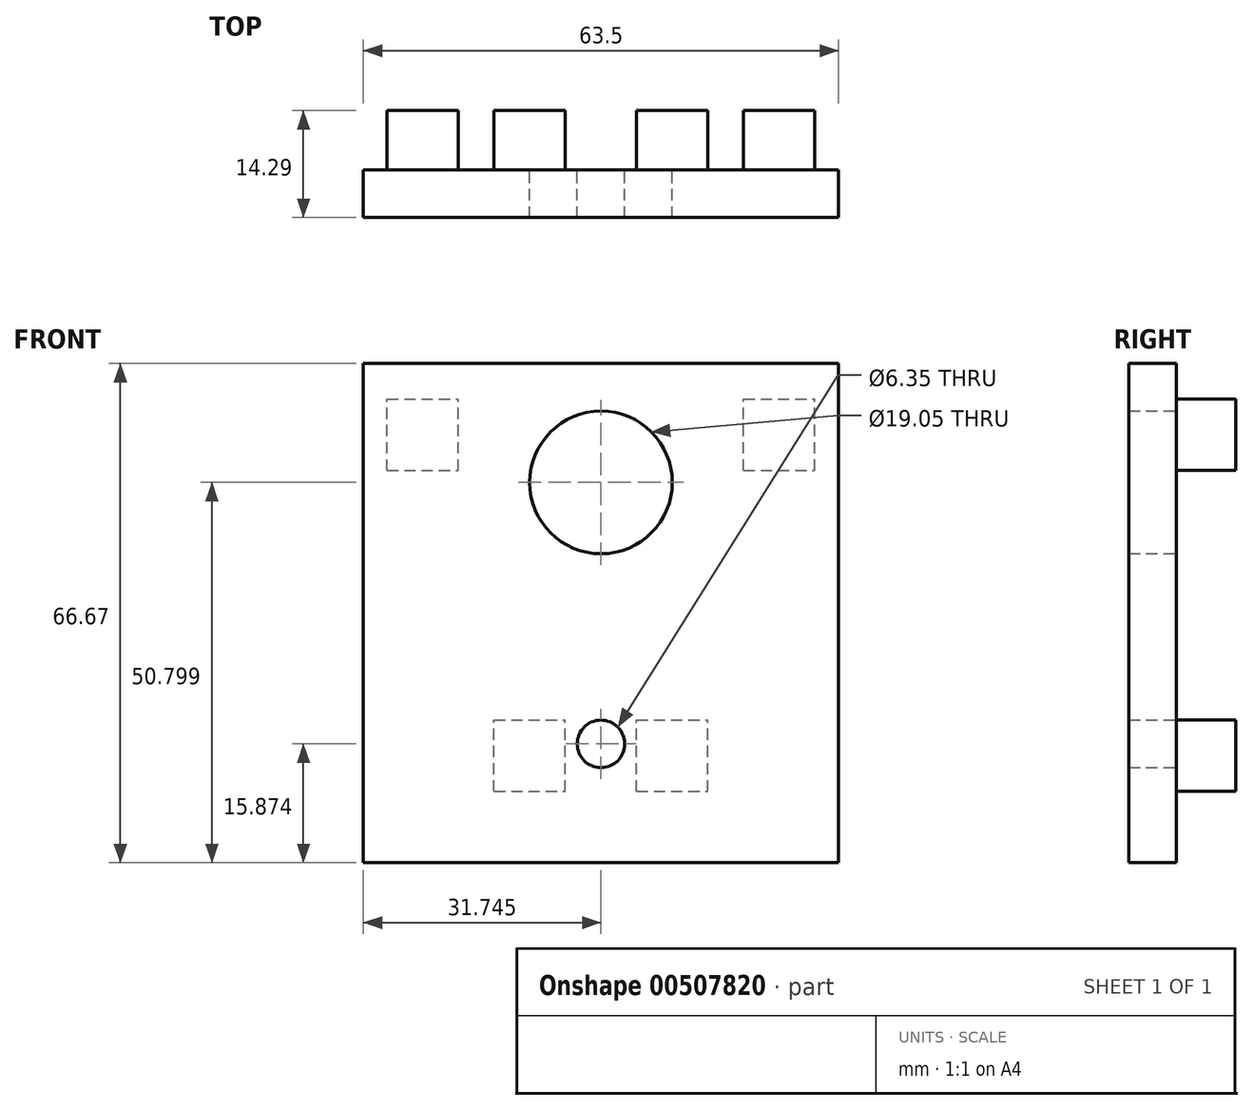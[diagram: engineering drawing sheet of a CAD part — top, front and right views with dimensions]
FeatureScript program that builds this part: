
annotation { "Feature Type Name" : "Feature", "Feature Type Description" : "" }
export const myFeature = defineFeature(function(context is Context, id is Id, definition is map)
    precondition{}
    {
        {
            var Q0;
            Q0=qCreatedBy(makeId("Front.planeOp"),FACE);
            var sketch = newSketch(context, id + "F0", { "sketchPlane" : qUnion([Q0])});
            skLineSegment(sketch, "E0.bottom", {"start": v(-27.9, 18.37) * mm, "end": v(35.6, 18.37) * mm});
            skLineSegment(sketch, "E0.top", {"start": v(-27.9, -45.13) * mm, "end": v(35.6, -45.13) * mm});
            skLineSegment(sketch, "E0.left", {"start": v(-27.9, 18.37) * mm, "end": v(-27.9, -45.13) * mm});
            skLineSegment(sketch, "E0.right", {"start": v(35.6, 18.37) * mm, "end": v(35.6, -45.13) * mm});
            skCircle(sketch, "E1", {"center": v(3.85, 2.5) * mm, "radius": 9.53 * mm});
            skLineSegment(sketch, "E2", {"start": v(-27.9, 2.5) * mm, "end": v(35.6, 2.5) * mm, "construction": true});
            skLineSegment(sketch, "E3.top", {"start": v(-27.9, -48.3) * mm, "end": v(35.6, -48.3) * mm});
            skLineSegment(sketch, "E3.left", {"start": v(-27.9, -45.13) * mm, "end": v(-27.9, -48.3) * mm});
            skLineSegment(sketch, "E3.right", {"start": v(35.6, -45.13) * mm, "end": v(35.6, -48.3) * mm});
            skLineSegment(sketch, "E4", {"start": v(-6.74, -45.13) * mm, "end": v(-6.74, -48.3) * mm});
            skLineSegment(sketch, "E5", {"start": v(14.43, -45.13) * mm, "end": v(14.43, -48.3) * mm});
            skCircle(sketch, "E6", {"center": v(3.85, -32.43) * mm, "radius": 3.18 * mm});
            skLineSegment(sketch, "E7", {"start": v(-10.44, 18.37) * mm, "end": v(-10.44, -45.13) * mm});
            skLineSegment(sketch, "E8", {"start": v(18.13, 18.37) * mm, "end": v(18.13, -45.13) * mm});
            skSolve(sketch);
        }
        {
            var Q0;
            {var subQ0=sQuery(id+"F0.wireOp",EDGE,"E3.left");Q0=makeQuery(id+"F0.imprint","IMPRINT",FACE,{"disambiguationData":[TD([[makeQuery(id+"F0.imprint","IMPRINT",EDGE,{"derivedFrom":subQ0}),1.0]])]});}
            var Q1;
            {var subQ0=sQuery(id+"F0.wireOp",EDGE,"E3.right");Q1=makeQuery(id+"F0.imprint","IMPRINT",FACE,{"disambiguationData":[TD([[makeQuery(id+"F0.imprint","IMPRINT",EDGE,{"derivedFrom":subQ0}),-1.0]])]});}
            var Q2;
            Q2=makeQuery(id+"F0.imprint","IMPRINT",FACE,{"disambiguationData":[TD([[makeQuery(id+"F0.imprint","IMPRINT",EDGE,{"derivedFrom":sQuery(id+"F0.wireOp",EDGE,"E0.bottom")}),-1.0]])]});
            var Q3;
            Q3=makeQuery(id+"F0.imprint","IMPRINT",FACE,{"disambiguationData":[TD([[makeQuery(id+"F0.imprint","IMPRINT",EDGE,{"derivedFrom":sQuery(id+"F0.wireOp",EDGE,"E1")}),-1.0]])]});
            var Q4;
            {var subQ0=sQuery(id+"F0.wireOp",EDGE,"E4");Q4=makeQuery(id+"F0.imprint","IMPRINT",FACE,{"disambiguationData":[TD([[makeQuery(id+"F0.imprint","IMPRINT",EDGE,{"derivedFrom":subQ0}),1.0]])]});}
            extrude(context, id + "F1", {"entities" : qUnion([Q0, Q1, Q2, Q3, Q4]), "endBound" : BoundingType.SYMMETRIC, "depth" : 6.35 * mm, "offsetDistance" : 25.4 * mm});
        }
        {
            var Q0;
            Q0=makeQuery(id+"F1.opExtrude","CAP_FACE",FACE,{"disambiguationData":[OSD([sQuery(id+"F0.wireOp",EDGE,"E0.bottom"),sQuery(id+"F0.wireOp",EDGE,"E0.left"),sQuery(id+"F0.wireOp",EDGE,"E0.right"),sQuery(id+"F0.wireOp",EDGE,"E1"),sQuery(id+"F0.wireOp",EDGE,"E0.top"),sQuery(id+"F0.wireOp",EDGE,"E3.top"),sQuery(id+"F0.wireOp",EDGE,"E3.left"),sQuery(id+"F0.wireOp",EDGE,"E3.right"),sQuery(id+"F0.wireOp",EDGE,"E4"),sQuery(id+"F0.wireOp",EDGE,"E5"),sQuery(id+"F0.wireOp",EDGE,"E6")])],"isStart":true});
            var sketch = newSketch(context, id + "F2", { "sketchPlane" : qUnion([Q0])});
            skLineSegment(sketch, "E9", {"start": v(-3.85, 2.5) * mm, "end": v(19.97, 2.5) * mm, "construction": true});
            skLineSegment(sketch, "E10", {"start": v(-3.85, 2.5) * mm, "end": v(-27.66, 2.5) * mm, "construction": true});
            skLineSegment(sketch, "E11", {"start": v(19.97, 2.5) * mm, "end": v(19.97, 8.85) * mm, "construction": true});
            skLineSegment(sketch, "E12", {"start": v(-27.66, 2.5) * mm, "end": v(-27.66, 8.85) * mm, "construction": true});
            skLineSegment(sketch, "E13.bottom", {"start": v(24.73, 4.09) * mm, "end": v(15.2, 4.09) * mm});
            skLineSegment(sketch, "E13.top", {"start": v(24.73, 13.61) * mm, "end": v(15.2, 13.61) * mm});
            skLineSegment(sketch, "E13.left", {"start": v(24.73, 4.09) * mm, "end": v(24.73, 13.61) * mm});
            skLineSegment(sketch, "E13.right", {"start": v(15.2, 4.09) * mm, "end": v(15.2, 13.61) * mm});
            skPoint(sketch, "E13.middle", {"position": v(19.97, 8.85) * mm});
            skLineSegment(sketch, "E14.bottom", {"start": v(-22.9, 4.09) * mm, "end": v(-32.42, 4.09) * mm});
            skLineSegment(sketch, "E14.top", {"start": v(-22.9, 13.61) * mm, "end": v(-32.42, 13.61) * mm});
            skLineSegment(sketch, "E14.left", {"start": v(-22.9, 4.09) * mm, "end": v(-22.9, 13.61) * mm});
            skLineSegment(sketch, "E14.right", {"start": v(-32.42, 4.09) * mm, "end": v(-32.42, 13.61) * mm});
            skPoint(sketch, "E14.middle", {"position": v(-27.66, 8.85) * mm});
            skLineSegment(sketch, "E15", {"start": v(-3.85, -32.43) * mm, "end": v(-3.85, -34.01) * mm, "construction": true});
            skLineSegment(sketch, "E16", {"start": v(-3.85, -34.01) * mm, "end": v(-13.37, -34.01) * mm, "construction": true});
            skLineSegment(sketch, "E17", {"start": v(-3.85, -34.01) * mm, "end": v(5.68, -34.01) * mm, "construction": true});
            skLineSegment(sketch, "E18.bottom", {"start": v(-8.6, -38.78) * mm, "end": v(-18.13, -38.78) * mm});
            skLineSegment(sketch, "E18.top", {"start": v(-8.6, -29.25) * mm, "end": v(-18.13, -29.25) * mm});
            skLineSegment(sketch, "E18.left", {"start": v(-8.6, -38.78) * mm, "end": v(-8.6, -29.25) * mm});
            skLineSegment(sketch, "E18.right", {"start": v(-18.13, -38.78) * mm, "end": v(-18.13, -29.25) * mm});
            skPoint(sketch, "E18.middle", {"position": v(-13.37, -34.01) * mm});
            skLineSegment(sketch, "E19.bottom", {"start": v(10.44, -38.78) * mm, "end": v(0.92, -38.78) * mm});
            skLineSegment(sketch, "E19.top", {"start": v(10.44, -29.25) * mm, "end": v(0.92, -29.25) * mm});
            skLineSegment(sketch, "E19.left", {"start": v(10.44, -38.78) * mm, "end": v(10.44, -29.25) * mm});
            skLineSegment(sketch, "E19.right", {"start": v(0.92, -38.78) * mm, "end": v(0.92, -29.25) * mm});
            skPoint(sketch, "E19.middle", {"position": v(5.68, -34.01) * mm});
            skSolve(sketch);
        }
        {
            var Q0;
            Q0 = qSketchRegion(id + "F2", true);
            extrude(context, id + "F3", {"entities" : qUnion([Q0]), "operationType" : NewBodyOperationType.ADD, "depth" : 7.94 * mm});
        }
    });
